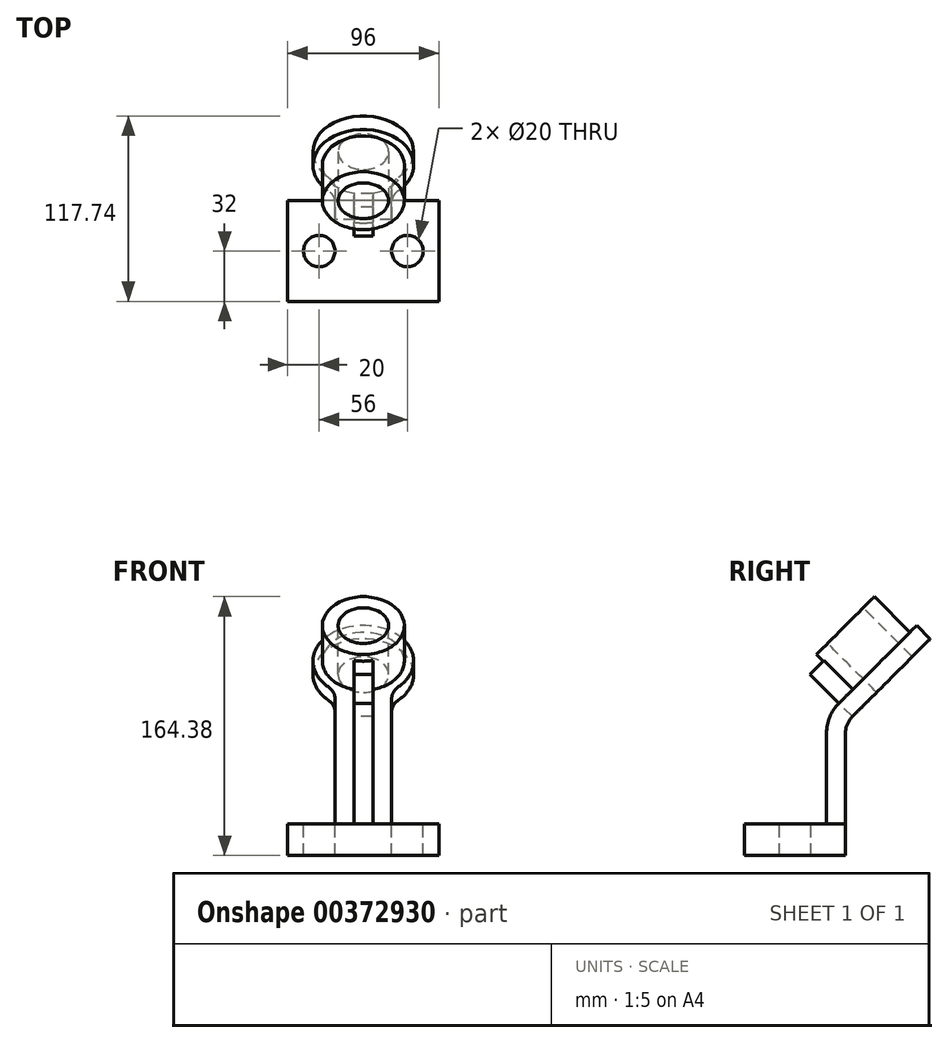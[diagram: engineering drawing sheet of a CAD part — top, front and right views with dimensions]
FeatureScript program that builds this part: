
annotation { "Feature Type Name" : "Feature", "Feature Type Description" : "" }
export const myFeature = defineFeature(function(context is Context, id is Id, definition is map)
    precondition{}
    {
        {
            var Q0;
            Q0=qCreatedBy(makeId("Top.planeOp"),FACE);
            var sketch = newSketch(context, id + "F0", { "sketchPlane" : qUnion([Q0])});
            skLineSegment(sketch, "E0.bottom", {"start": v(48, 32) * mm, "end": v(-48, 32) * mm});
            skLineSegment(sketch, "E0.top", {"start": v(48, -32) * mm, "end": v(-48, -32) * mm});
            skLineSegment(sketch, "E0.left", {"start": v(48, 32) * mm, "end": v(48, -32) * mm});
            skLineSegment(sketch, "E0.right", {"start": v(-48, 32) * mm, "end": v(-48, -32) * mm});
            skPoint(sketch, "E0.middle", {"position": v(0, 0) * mm});
            skCircle(sketch, "E1", {"center": v(-28, 0) * mm, "radius": 10 * mm});
            skCircle(sketch, "E2.MirrorC", {"center": v(28, 0) * mm, "radius": 10 * mm});
            skSolve(sketch);
        }
        {
            var Q0;
            Q0=makeQuery(id+"F0.imprint","IMPRINT",FACE,{"disambiguationData":[TD([[makeQuery(id+"F0.imprint","IMPRINT",EDGE,{"derivedFrom":sQuery(id+"F0.wireOp",EDGE,"E0.bottom")}),1.0]])]});
            extrude(context, id + "F1", {"entities" : qUnion([Q0]), "oppositeDirection" : true, "depth" : 20 * mm});
        }
        {
            var Q0;
            Q0=qCreatedBy(makeId("Right.planeOp"),FACE);
            var sketch = newSketch(context, id + "F2", { "sketchPlane" : qUnion([Q0])});
            skLineSegment(sketch, "E3", {"start": v(43.31, 137.31) * mm, "end": v(50.38, 144.38) * mm});
            skLineSegment(sketch, "E4", {"start": v(50.38, 144.38) * mm, "end": v(73.01, 121.76) * mm});
            skLineSegment(sketch, "E5", {"start": v(73.01, 121.76) * mm, "end": v(65.94, 114.69) * mm});
            skLineSegment(sketch, "E6", {"start": v(73.01, 121.76) * mm, "end": v(77.25, 126) * mm});
            skLineSegment(sketch, "E7", {"start": v(77.25, 126) * mm, "end": v(85.74, 117.51) * mm});
            skPoint(sketch, "E8", {"position": v(32, 126) * mm});
            skLineSegment(sketch, "E9", {"start": v(32, 126) * mm, "end": v(63.11, 94.89) * mm, "construction": true});
            skLineSegment(sketch, "E10", {"start": v(32, -24.57) * mm, "end": v(32, 0) * mm});
            skLineSegment(sketch, "E11", {"start": v(32, 126) * mm, "end": v(32, -15.65) * mm, "construction": true});
            skPoint(sketch, "E12.orphan", {"position": v(13.62, 107.62) * mm});
            skLineSegment(sketch, "E13", {"start": v(43.31, 137.31) * mm, "end": v(65.94, 114.69) * mm});
            skLineSegment(sketch, "E14", {"start": v(65.94, 114.69) * mm, "end": v(74.43, 106.2) * mm});
            skLineSegment(sketch, "E15", {"start": v(74.43, 106.2) * mm, "end": v(85.74, 117.51) * mm});
            skSolve(sketch);
        }
        {
            var Q0;
            Q0=makeQuery(id+"F2.imprint","IMPRINT",FACE,{"disambiguationData":[TD([[makeQuery(id+"F2.imprint","IMPRINT",EDGE,{"derivedFrom":sQuery(id+"F2.wireOp",EDGE,"E3")}),-1.0]])]});
            var Q1;
            Q1=makeQuery(id+"F2.imprint","IMPRINT",FACE,{"disambiguationData":[TD([[makeQuery(id+"F2.imprint","IMPRINT",EDGE,{"derivedFrom":sQuery(id+"F2.wireOp",EDGE,"E5")}),1.0]])]});
            var Q2;
            Q2=sQuery(id+"F2.wireOp",EDGE,"E9");
            revolve(context, id + "F3", {"entities" : qUnion([Q0, Q1]), "axis" : qUnion([Q2]), "revolveType" : RevolveType.FULL});
        }
        {
            var Q0;
            Q0=qCreatedBy(makeId("Right.planeOp"),FACE);
            var sketch = newSketch(context, id + "F4", { "sketchPlane" : qUnion([Q0])});
            skLineSegment(sketch, "E16", {"start": v(32, 0) * mm, "end": v(32, 57.56) * mm});
            skArc(sketch, "E17", {"start": v(32, 57.56) * mm, "mid": v(33.14, 63.3) * mm, "end": v(36.4, 68.17) * mm});
            skLineSegment(sketch, "E18", {"start": v(49.22, 81) * mm, "end": v(36.4, 68.17) * mm});
            skArc(sketch, "E19.1", {"start": v(20, 57.56) * mm, "mid": v(22.06, 67.9) * mm, "end": v(27.9, 76.65) * mm});
            skLineSegment(sketch, "E19.2", {"start": v(20, 0) * mm, "end": v(20, 57.56) * mm});
            skLineSegment(sketch, "E20.0", {"start": v(-32, -20) * mm, "end": v(-32, 0) * mm});
            skLineSegment(sketch, "E21", {"start": v(-32, 0) * mm, "end": v(-32, 9.42) * mm});
            skArc(sketch, "E22", {"start": v(-32, 9.42) * mm, "mid": v(-12.92, 30.2) * mm, "end": v(-6, 57.56) * mm});
            skArc(sketch, "E23", {"start": v(-6, 57.56) * mm, "mid": v(-1.97, 77.84) * mm, "end": v(9.52, 95.04) * mm});
            skLineSegment(sketch, "E24", {"start": v(36.4, 68.17) * mm, "end": v(9.52, 95.04) * mm});
            skLineSegment(sketch, "E25", {"start": v(9.52, 95.04) * mm, "end": v(22.35, 107.87) * mm});
            skLineSegment(sketch, "E26", {"start": v(22.35, 107.87) * mm, "end": v(49.22, 81) * mm});
            skPoint(sketch, "E27.orphan", {"position": v(-63.56, 0) * mm});
            skLineSegment(sketch, "E28", {"start": v(-32, 0) * mm, "end": v(32, 0) * mm});
            skLineSegment(sketch, "E29", {"start": v(27.9, 76.65) * mm, "end": v(40.74, 89.48) * mm});
            skSolve(sketch);
        }
        {
            var Q0;
            {var subQ2=sQuery(id+"F4.wireOp",EDGE,"E25");Q0=makeQuery(id+"F4.imprint","IMPRINT",FACE,{"disambiguationData":[TD([[makeQuery(id+"F4.imprint","IMPRINT",EDGE,{"derivedFrom":subQ2}),-1.0]])]});}
            var Q1;
            {var subQ2=sQuery(id+"F4.wireOp",EDGE,"E19.1");Q1=makeQuery(id+"F4.imprint","IMPRINT",FACE,{"disambiguationData":[TD([[makeQuery(id+"F4.imprint","IMPRINT",EDGE,{"derivedFrom":subQ2}),1.0]])]});}
            extrude(context, id + "F5", {"entities" : qUnion([Q0, Q1]), "endBound" : BoundingType.SYMMETRIC, "depth" : 12 * mm, "hasSecondDirection" : true, "secondDirectionOppositeDirection" : true, "secondDirectionDepth" : 6 * mm});
        }
        {
            var Q0;
            {var subQ3=sQuery(id+"F4.wireOp",EDGE,"E16");Q0=makeQuery(id+"F4.imprint","IMPRINT",FACE,{"disambiguationData":[TD([[makeQuery(id+"F4.imprint","IMPRINT",EDGE,{"derivedFrom":subQ3}),1.0]])]});}
            var Q1;
            {var subQ0=sQuery(id+"F4.wireOp",EDGE,"E18");Q1=makeQuery(id+"F4.imprint","IMPRINT",FACE,{"disambiguationData":[TD([[makeQuery(id+"F4.imprint","IMPRINT",EDGE,{"derivedFrom":subQ0}),-1.0]])]});}
            extrude(context, id + "F6", {"entities" : qUnion([Q0, Q1]), "endBound" : BoundingType.SYMMETRIC, "depth" : 36 * mm});
        }
        {
            var Q0;
            Q0=makeQuery(id+"F6.opExtrude","SWEPT_BODY",BODY,{"disambiguationData":[OSD([sQuery(id+"F4.wireOp",EDGE,"E16"),sQuery(id+"F4.wireOp",EDGE,"E17"),sQuery(id+"F4.wireOp",EDGE,"E18"),sQuery(id+"F4.wireOp",EDGE,"E19.1"),sQuery(id+"F4.wireOp",EDGE,"E19.2"),sQuery(id+"F4.wireOp",EDGE,"E26"),sQuery(id+"F4.wireOp",EDGE,"E28"),sQuery(id+"F4.wireOp",EDGE,"E29")])]});
            var Q1;
            Q1=makeQuery(id+"F1.opExtrude","SWEPT_BODY",BODY,{"disambiguationData":[OSD([sQuery(id+"F0.wireOp",EDGE,"E0.bottom"),sQuery(id+"F0.wireOp",EDGE,"E0.top"),sQuery(id+"F0.wireOp",EDGE,"E0.left"),sQuery(id+"F0.wireOp",EDGE,"E0.right"),sQuery(id+"F0.wireOp",EDGE,"E1"),sQuery(id+"F0.wireOp",EDGE,"E2.MirrorC")])]});
            var Q2;
            Q2=makeQuery(id+"F3.opRevolve","SWEPT_BODY",BODY,{"disambiguationData":[OSD([sQuery(id+"F2.wireOp",EDGE,"E3"),sQuery(id+"F2.wireOp",EDGE,"E4"),sQuery(id+"F2.wireOp",EDGE,"E6"),sQuery(id+"F2.wireOp",EDGE,"E7"),sQuery(id+"F2.wireOp",EDGE,"E13"),sQuery(id+"F2.wireOp",EDGE,"E14"),sQuery(id+"F2.wireOp",EDGE,"E15")])]});
            var Q3;
            Q3=makeQuery(id+"F5.opExtrude","SWEPT_BODY",BODY,{"disambiguationData":[OSD([sQuery(id+"F4.wireOp",EDGE,"E19.1"),sQuery(id+"F4.wireOp",EDGE,"E19.2"),sQuery(id+"F4.wireOp",EDGE,"E21"),sQuery(id+"F4.wireOp",EDGE,"E22"),sQuery(id+"F4.wireOp",EDGE,"E23"),sQuery(id+"F4.wireOp",EDGE,"E25"),sQuery(id+"F4.wireOp",EDGE,"E26"),sQuery(id+"F4.wireOp",EDGE,"E28"),sQuery(id+"F4.wireOp",EDGE,"E29")])]});
            booleanBodies(context, id + "F7", {"operationType" : BooleanOperationType.UNION, "tools" : qUnion([Q0, Q1, Q2, Q3])});
        }
        {
            var Q0;
            Q0=makeQuery(id+"F7.opBoolean","INTERSECT",EDGE,{"derivedFrom":[makeQuery(id+"F3.opRevolve","SWEPT_FACE",FACE,{"disambiguationData":[OSD([sQuery(id+"F2.wireOp",EDGE,"E7")])]}),makeQuery(id+"F6.opExtrude","CAP_FACE",FACE,{"disambiguationData":[OSD([sQuery(id+"F4.wireOp",EDGE,"E16"),sQuery(id+"F4.wireOp",EDGE,"E17"),sQuery(id+"F4.wireOp",EDGE,"E18"),sQuery(id+"F4.wireOp",EDGE,"E19.1"),sQuery(id+"F4.wireOp",EDGE,"E19.2"),sQuery(id+"F4.wireOp",EDGE,"E26"),sQuery(id+"F4.wireOp",EDGE,"E28"),sQuery(id+"F4.wireOp",EDGE,"E29")])],"isStart":false})]});
            var Q1;
            Q1=makeQuery(id+"F7.opBoolean","INTERSECT",EDGE,{"derivedFrom":[makeQuery(id+"F3.opRevolve","SWEPT_FACE",FACE,{"disambiguationData":[OSD([sQuery(id+"F2.wireOp",EDGE,"E7")])]}),makeQuery(id+"F6.opExtrude","CAP_FACE",FACE,{"disambiguationData":[OSD([sQuery(id+"F4.wireOp",EDGE,"E16"),sQuery(id+"F4.wireOp",EDGE,"E17"),sQuery(id+"F4.wireOp",EDGE,"E18"),sQuery(id+"F4.wireOp",EDGE,"E19.1"),sQuery(id+"F4.wireOp",EDGE,"E19.2"),sQuery(id+"F4.wireOp",EDGE,"E26"),sQuery(id+"F4.wireOp",EDGE,"E28"),sQuery(id+"F4.wireOp",EDGE,"E29")])],"isStart":true})]});
            fillet(context, id + "F8", {"entities" : qUnion([Q0, Q1]), "radius" : 15 * mm, "tangentPropagation" : true, "allowEdgeOverflow" : false});
        }
    });
